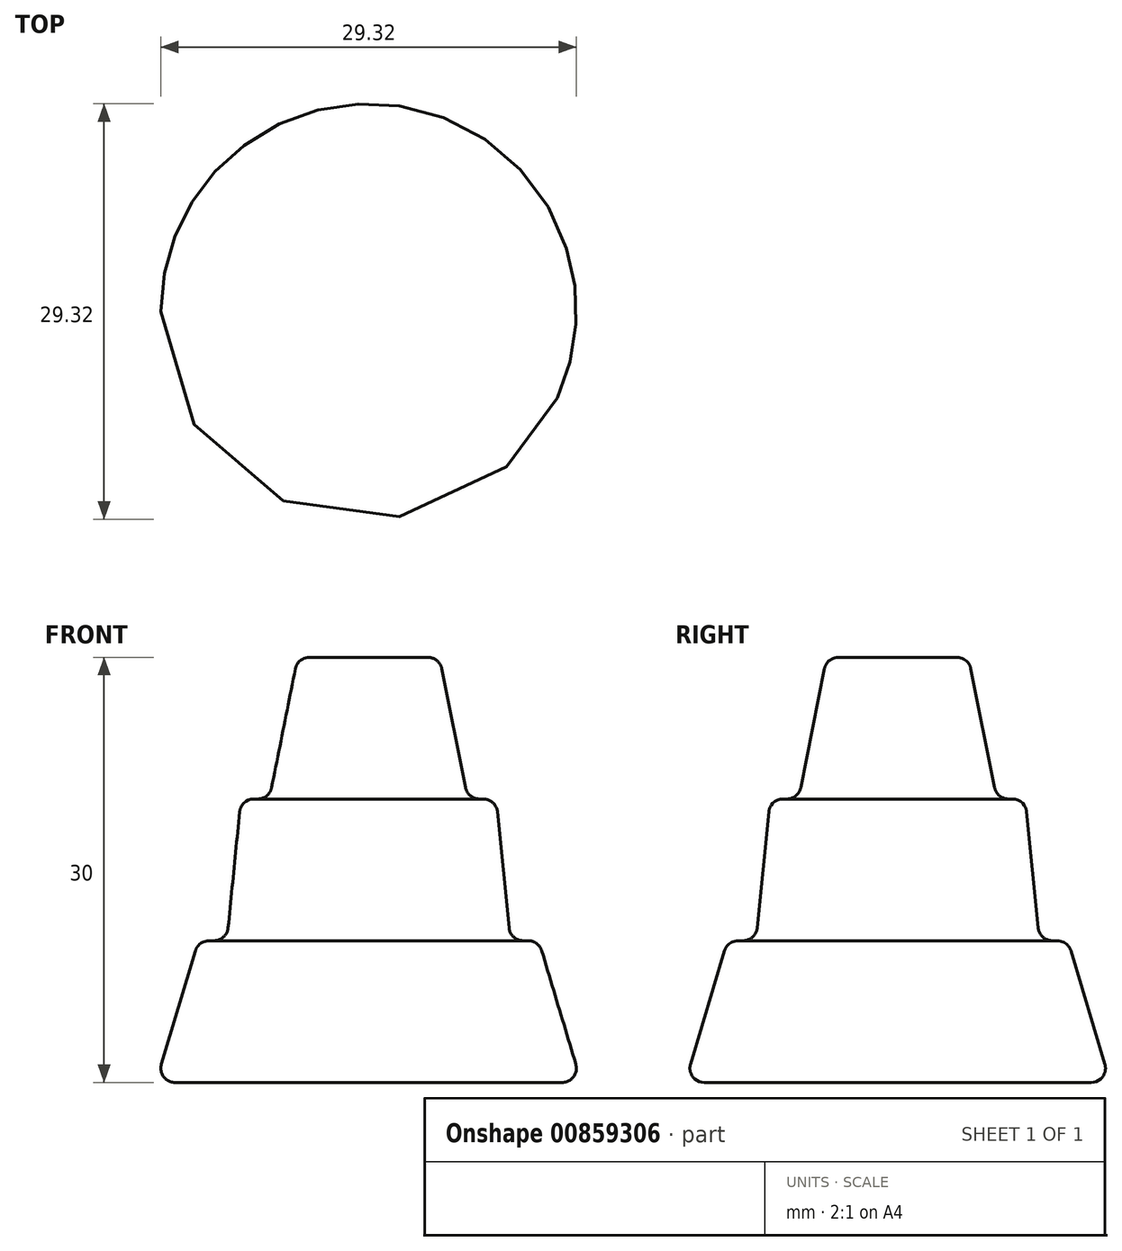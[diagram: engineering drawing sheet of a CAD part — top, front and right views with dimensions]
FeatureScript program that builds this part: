
annotation { "Feature Type Name" : "Feature", "Feature Type Description" : "" }
export const myFeature = defineFeature(function(context is Context, id is Id, definition is map)
    precondition{}
    {
        {
            var Q0;
            Q0=qCreatedBy(makeId("Front.planeOp"),FACE);
            var sketch = newSketch(context, id + "F0", { "sketchPlane" : qUnion([Q0])});
            skLineSegment(sketch, "E0", {"start": v(0, 10) * mm, "end": v(0, 0) * mm});
            skLineSegment(sketch, "E1", {"start": v(10, 10) * mm, "end": v(12, 10) * mm});
            skLineSegment(sketch, "E2", {"start": v(12, 10) * mm, "end": v(15, 0) * mm});
            skLineSegment(sketch, "E3", {"start": v(15, 0) * mm, "end": v(0, 0) * mm});
            skLineSegment(sketch, "E4", {"start": v(0, 10) * mm, "end": v(0, 20) * mm});
            skLineSegment(sketch, "E5", {"start": v(7, 20) * mm, "end": v(9, 20) * mm});
            skLineSegment(sketch, "E6", {"start": v(9, 20) * mm, "end": v(10, 10) * mm});
            skLineSegment(sketch, "E7", {"start": v(0, 20) * mm, "end": v(0, 30) * mm});
            skLineSegment(sketch, "E8", {"start": v(0, 30) * mm, "end": v(5, 30) * mm});
            skLineSegment(sketch, "E9", {"start": v(5, 30) * mm, "end": v(7, 20) * mm});
            skSolve(sketch);
        }
        {
            var Q0;
            Q0=makeQuery(id+"F0.imprint","IMPRINT",FACE,{"disambiguationData":[TD([[makeQuery(id+"F0.imprint","IMPRINT",EDGE,{"derivedFrom":sQuery(id+"F0.wireOp",EDGE,"E0")}),1.0]])]});
            var Q1;
            Q1=sQuery(id+"F0.wireOp",EDGE,"E0");
            revolve(context, id + "F1", {"surfaceOperationType" : NewSurfaceOperationType.NEW, "entities" : qUnion([Q0]), "axis" : qUnion([Q1]), "revolveType" : RevolveType.FULL});
        }
        {
            var Q0;
            Q0=makeQuery(id+"F1.opRevolve","SWEPT_EDGE",EDGE,{"disambiguationData":[OSD([sQuery(id+"F0.wireOp",EDGE,"E1"),sQuery(id+"F0.wireOp",EDGE,"E2")])]});
            var Q1;
            Q1=makeQuery(id+"F1.opRevolve","SWEPT_EDGE",EDGE,{"disambiguationData":[OSD([sQuery(id+"F0.wireOp",EDGE,"E1"),sQuery(id+"F0.wireOp",EDGE,"E6")])]});
            var Q2;
            Q2=makeQuery(id+"F1.opRevolve","SWEPT_EDGE",EDGE,{"disambiguationData":[OSD([sQuery(id+"F0.wireOp",EDGE,"E5"),sQuery(id+"F0.wireOp",EDGE,"E6")])]});
            var Q3;
            Q3=makeQuery(id+"F1.opRevolve","SWEPT_EDGE",EDGE,{"disambiguationData":[OSD([sQuery(id+"F0.wireOp",EDGE,"E2"),sQuery(id+"F0.wireOp",EDGE,"E3")])]});
            var Q4;
            Q4=makeQuery(id+"F1.opRevolve","SWEPT_EDGE",EDGE,{"disambiguationData":[OSD([sQuery(id+"F0.wireOp",EDGE,"E5"),sQuery(id+"F0.wireOp",EDGE,"E9")])]});
            var Q5;
            Q5=makeQuery(id+"F1.opRevolve","SWEPT_EDGE",EDGE,{"disambiguationData":[OSD([sQuery(id+"F0.wireOp",EDGE,"E8"),sQuery(id+"F0.wireOp",EDGE,"E9")])]});
            fillet(context, id + "F2", {"entities" : qUnion([Q0, Q1, Q2, Q3, Q4, Q5]), "radius" : 1 * mm, "tangentPropagation" : true, "allowEdgeOverflow" : false});
        }
    });
